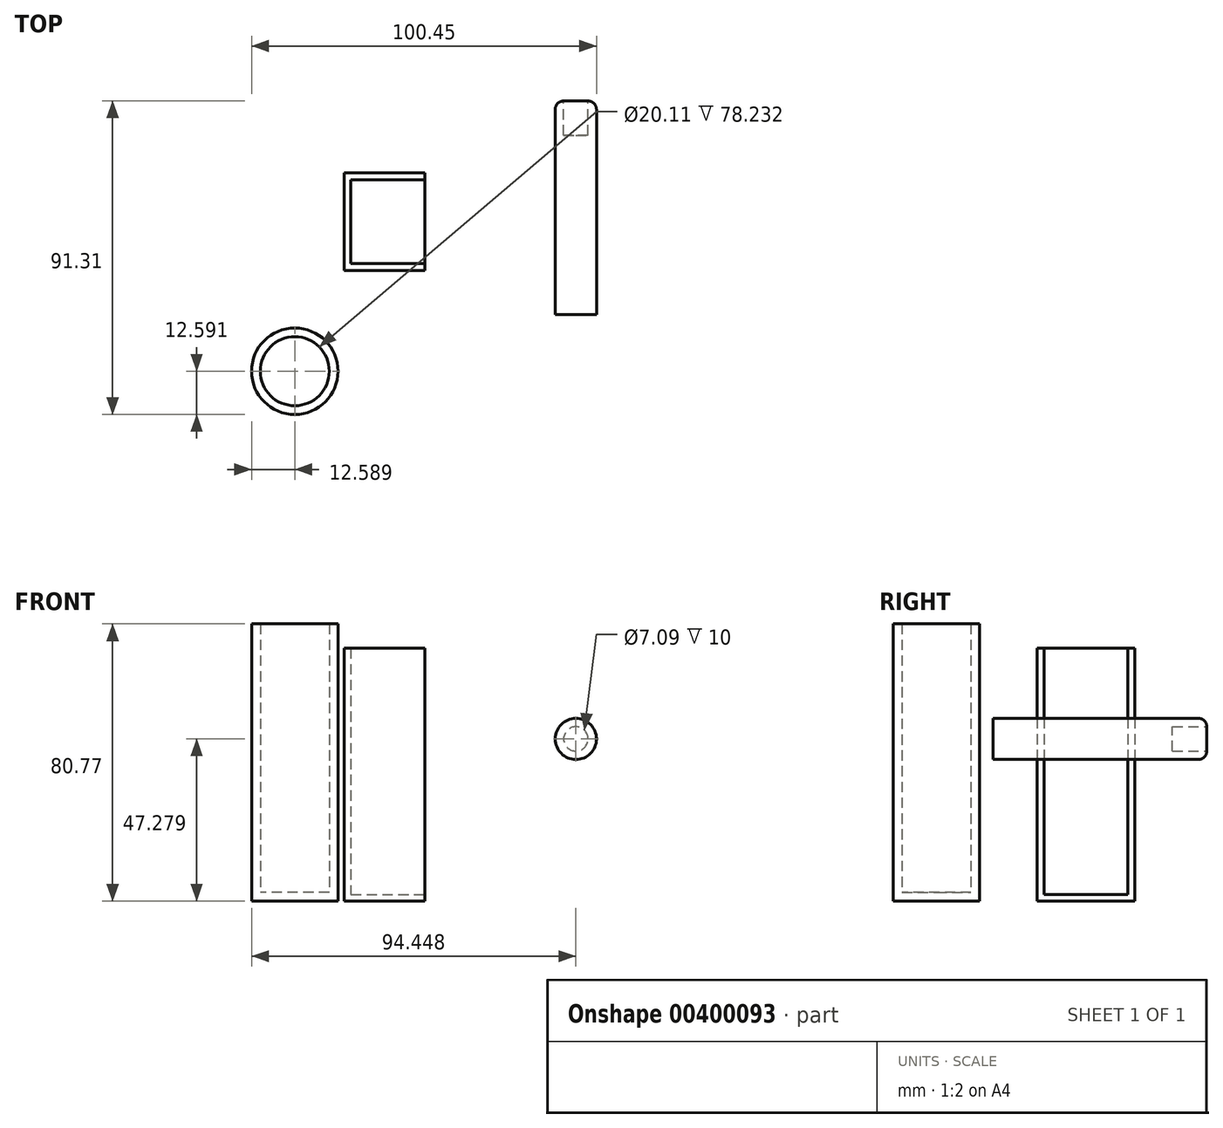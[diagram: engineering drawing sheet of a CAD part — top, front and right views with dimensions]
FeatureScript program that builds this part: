
annotation { "Feature Type Name" : "Feature", "Feature Type Description" : "" }
export const myFeature = defineFeature(function(context is Context, id is Id, definition is map)
    precondition{}
    {
        {
            var Q0;
            Q0=qCreatedBy(makeId("Top.planeOp"),FACE);
            var sketch = newSketch(context, id + "F0", { "sketchPlane" : qUnion([Q0])});
            skLineSegment(sketch, "E0.bottom", {"start": v(-42.06, 41.24) * mm, "end": v(-18.56, 41.24) * mm});
            skLineSegment(sketch, "E0.top", {"start": v(-42.06, 12.81) * mm, "end": v(-18.56, 12.81) * mm});
            skLineSegment(sketch, "E0.left", {"start": v(-42.06, 41.24) * mm, "end": v(-42.06, 12.81) * mm});
            skLineSegment(sketch, "E0.right", {"start": v(-18.56, 41.24) * mm, "end": v(-18.56, 12.81) * mm});
            skSolve(sketch);
        }
        {
            var Q0;
            Q0=makeQuery(id+"F0.imprint","IMPRINT",FACE,{"disambiguationData":[TD([[makeQuery(id+"F0.imprint","IMPRINT",EDGE,{"derivedFrom":sQuery(id+"F0.wireOp",EDGE,"E0.bottom")}),-1.0]])]});
            extrude(context, id + "F1", {"entities" : qUnion([Q0]), "depth" : 73.66 * mm});
        }
        {
            var Q0;
            Q0=makeQuery(id+"F1.opExtrude","CAP_FACE",FACE,{"disambiguationData":[OSD([sQuery(id+"F0.wireOp",EDGE,"E0.bottom"),sQuery(id+"F0.wireOp",EDGE,"E0.top"),sQuery(id+"F0.wireOp",EDGE,"E0.left"),sQuery(id+"F0.wireOp",EDGE,"E0.right")])],"isStart":false});
            var Q1;
            Q1=makeQuery(id+"F1.opExtrude","SWEPT_FACE",FACE,{"disambiguationData":[OSD([sQuery(id+"F0.wireOp",EDGE,"E0.right")])]});
            shell(context, id + "F2", {"entities" : qUnion([Q0, Q1]), "thickness" : 2 * mm});
        }
        {
            var Q0;
            Q0=qCreatedBy(makeId("Front.planeOp"),FACE);
            var sketch = newSketch(context, id + "F3", { "sketchPlane" : qUnion([Q0])});
            skCircle(sketch, "E1", {"center": v(25.46, 47.28) * mm, "radius": 6 * mm});
            skLineSegment(sketch, "E2.bottom", {"start": v(41.91, 61.13) * mm, "end": v(6.93, 61.13) * mm});
            skLineSegment(sketch, "E2.top", {"start": v(41.91, 39.49) * mm, "end": v(6.93, 39.49) * mm});
            skLineSegment(sketch, "E2.left", {"start": v(41.91, 61.13) * mm, "end": v(41.91, 39.49) * mm});
            skLineSegment(sketch, "E2.right", {"start": v(6.93, 61.13) * mm, "end": v(6.93, 39.49) * mm});
            skSolve(sketch);
        }
        {
            var Q0;
            Q0=makeQuery(id+"F3.imprint","IMPRINT",FACE,{"disambiguationData":[TD([[makeQuery(id+"F3.imprint","IMPRINT",EDGE,{"derivedFrom":sQuery(id+"F3.wireOp",EDGE,"E1")}),1.0]])]});
            extrude(context, id + "F4", {"entities" : qUnion([Q0]), "oppositeDirection" : true, "depth" : 62.23 * mm});
        }
        {
            var Q0;
            Q0=qCreatedBy(makeId("Top.planeOp"),FACE);
            var sketch = newSketch(context, id + "F5", { "sketchPlane" : qUnion([Q0])});
            skCircle(sketch, "E3", {"center": v(-56.4, -16.49) * mm, "radius": 12.6 * mm});
            skSolve(sketch);
        }
        {
            var Q0;
            Q0=makeQuery(id+"F5.imprint","IMPRINT",FACE,{"disambiguationData":[TD([[makeQuery(id+"F5.imprint","IMPRINT",EDGE,{"derivedFrom":sQuery(id+"F5.wireOp",EDGE,"E3")}),1.0]])]});
            extrude(context, id + "F6", {"entities" : qUnion([Q0]), "depth" : 80.77 * mm});
        }
        {
            var Q0;
            Q0=makeQuery(id+"F6.opExtrude","CAP_FACE",FACE,{"disambiguationData":[OSD([sQuery(id+"F5.wireOp",EDGE,"E3")])],"isStart":false});
            shell(context, id + "F7", {"entities" : qUnion([Q0]), "thickness" : 2.54 * mm});
        }
        {
            var Q0;
            Q0=makeQuery(id+"F4.opExtrude","CAP_FACE",FACE,{"disambiguationData":[OSD([sQuery(id+"F3.wireOp",EDGE,"E1")])],"isStart":false});
            fillet(context, id + "F8", {"entities" : qUnion([Q0]), "radius" : 2.45 * mm, "tangentPropagation" : true, "allowEdgeOverflow" : false});
        }
        {
            var Q0;
            Q0=makeQuery(id+"F4.opExtrude","CAP_FACE",FACE,{"disambiguationData":[OSD([sQuery(id+"F3.wireOp",EDGE,"E1")])],"isStart":false});
            extrude(context, id + "F9", {"entities" : qUnion([Q0]), "operationType" : NewBodyOperationType.ADD, "oppositeDirection" : true, "depth" : 6.6 * mm});
        }
        {
            var Q0;
            Q0=makeQuery(id+"F4.opExtrude","CAP_FACE",FACE,{"disambiguationData":[OSD([sQuery(id+"F3.wireOp",EDGE,"E1")])],"isStart":false});
            extrude(context, id + "F10", {"entities" : qUnion([Q0]), "operationType" : NewBodyOperationType.ADD, "oppositeDirection" : true, "depth" : 6.35 * mm});
        }
        {
            var Q0;
            Q0=makeQuery(id+"F4.opExtrude","CAP_FACE",FACE,{"disambiguationData":[OSD([sQuery(id+"F3.wireOp",EDGE,"E1")])],"isStart":false});
            extrude(context, id + "F11", {"entities" : qUnion([Q0]), "operationType" : NewBodyOperationType.ADD, "oppositeDirection" : true, "depth" : 16.5 * mm});
        }
        {
            var Q0;
            Q0=makeQuery(id+"F4.opExtrude","CAP_FACE",FACE,{"disambiguationData":[OSD([sQuery(id+"F3.wireOp",EDGE,"E1")])],"isStart":false});
            extrude(context, id + "F12", {"entities" : qUnion([Q0]), "operationType" : NewBodyOperationType.REMOVE, "oppositeDirection" : true, "depth" : 10 * mm});
        }
    });
